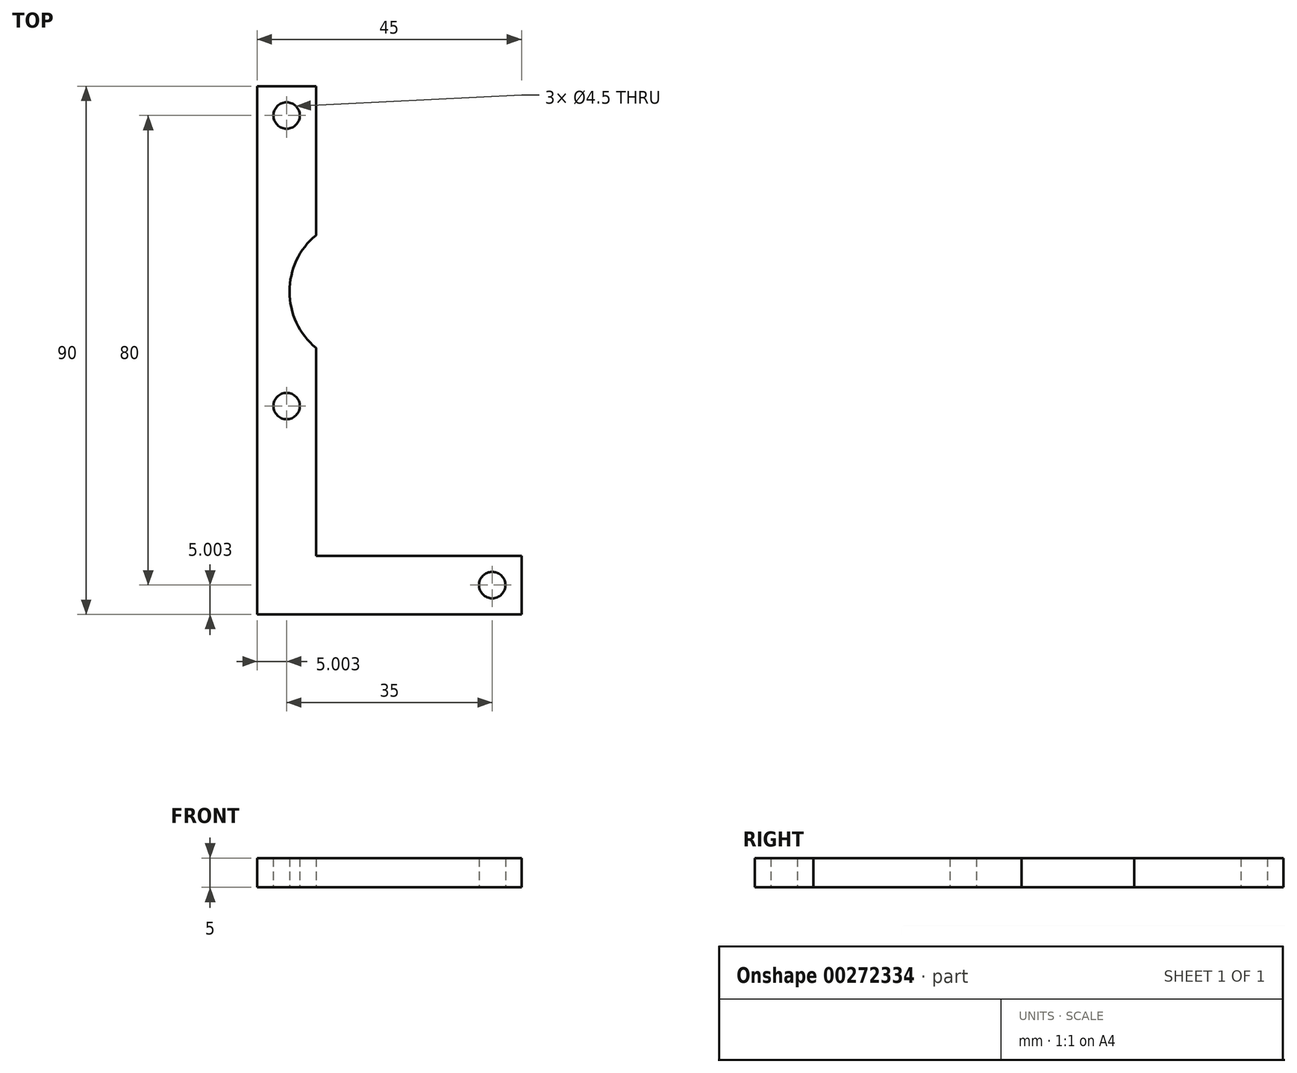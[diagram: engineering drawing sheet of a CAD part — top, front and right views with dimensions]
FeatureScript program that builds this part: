
annotation { "Feature Type Name" : "Feature", "Feature Type Description" : "" }
export const myFeature = defineFeature(function(context is Context, id is Id, definition is map)
    precondition{}
    {
        {
            var Q0;
            Q0=qCreatedBy(makeId("Top.planeOp"),FACE);
            var sketch = newSketch(context, id + "F0", { "sketchPlane" : qUnion([Q0])});
            skLineSegment(sketch, "E0.bottom", {"start": v(-56.54, 38.24) * mm, "end": v(-46.54, 38.24) * mm});
            skLineSegment(sketch, "E0.top", {"start": v(-56.54, -51.76) * mm, "end": v(-46.54, -51.76) * mm});
            skLineSegment(sketch, "E0.left", {"start": v(-56.54, 38.24) * mm, "end": v(-56.54, -51.76) * mm});
            skLineSegment(sketch, "E0.right", {"start": v(-46.54, 38.24) * mm, "end": v(-46.54, -41.76) * mm});
            skLineSegment(sketch, "E1.bottom", {"start": v(-46.54, -51.76) * mm, "end": v(-11.54, -51.76) * mm});
            skLineSegment(sketch, "E1.top", {"start": v(-46.54, -41.76) * mm, "end": v(-11.54, -41.76) * mm});
            skLineSegment(sketch, "E1.right", {"start": v(-11.54, -51.76) * mm, "end": v(-11.54, -41.76) * mm});
            skCircle(sketch, "E2", {"center": v(-38.54, 3.24) * mm, "radius": 12.5 * mm});
            skLineSegment(sketch, "E3", {"start": v(-51.54, 38.24) * mm, "end": v(-51.54, -51.76) * mm, "construction": true});
            skCircle(sketch, "E4", {"center": v(-51.54, 33.24) * mm, "radius": 2.25 * mm});
            skLineSegment(sketch, "E5", {"start": v(-11.54, -46.76) * mm, "end": v(-56.54, -46.76) * mm, "construction": true});
            skCircle(sketch, "E6", {"center": v(-16.54, -46.76) * mm, "radius": 2.25 * mm});
            skPoint(sketch, "E7", {"position": v(-51.54, -46.76) * mm});
            skPoint(sketch, "E8", {"position": v(-46.54, -6.36) * mm});
            skPoint(sketch, "E9", {"position": v(-46.54, 12.85) * mm});
            skCircle(sketch, "E10", {"center": v(-51.54, -16.26) * mm, "radius": 2.25 * mm});
            skSolve(sketch);
        }
        {
            var Q0;
            {var subQ1=sQuery(id+"F0.wireOp",EDGE,"E0.bottom");Q0=makeQuery(id+"F0.imprint","IMPRINT",FACE,{"disambiguationData":[TD([[makeQuery(id+"F0.imprint","IMPRINT",EDGE,{"derivedFrom":subQ1}),-1.0]])]});}
            extrude(context, id + "F1", {"entities" : qUnion([Q0]), "depth" : 5 * mm});
        }
    });
